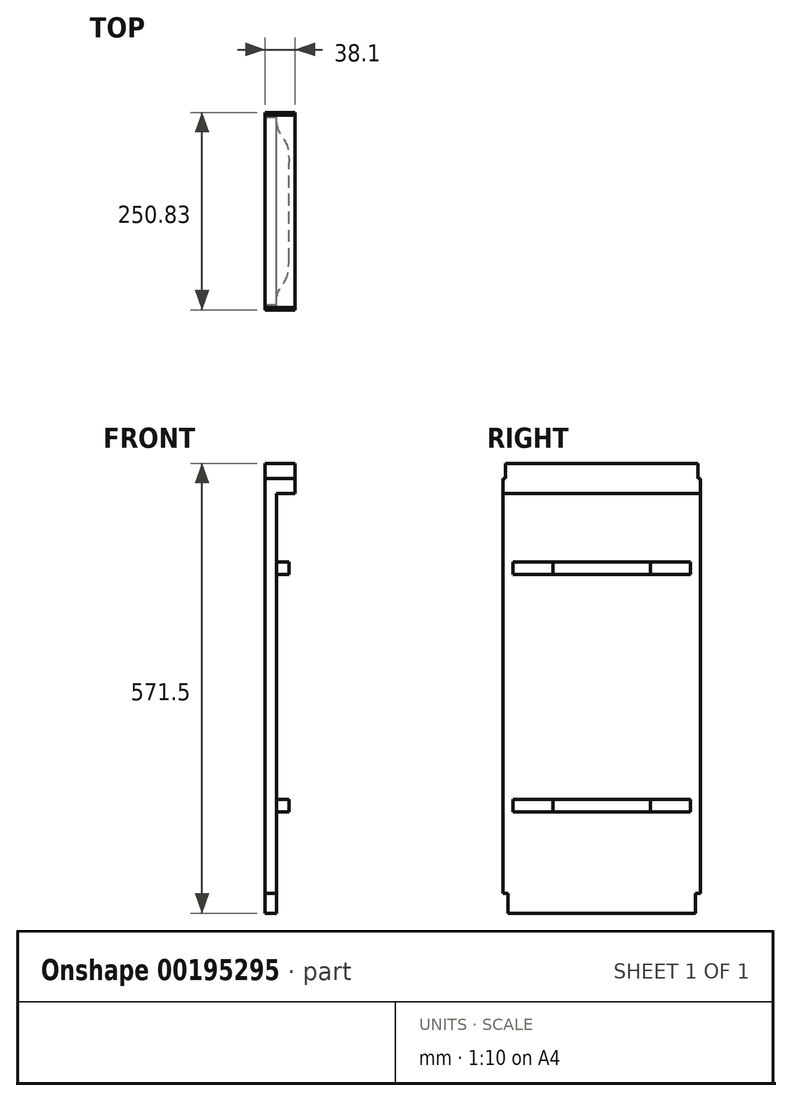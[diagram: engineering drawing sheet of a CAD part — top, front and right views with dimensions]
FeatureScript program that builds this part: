
annotation { "Feature Type Name" : "Feature", "Feature Type Description" : "" }
export const myFeature = defineFeature(function(context is Context, id is Id, definition is map)
    precondition{}
    {
        {
            var Q0;
            Q0=qCreatedBy(makeId("Front.planeOp"),FACE);
            var sketch = newSketch(context, id + "F0", { "sketchPlane" : qUnion([Q0])});
            skLineSegment(sketch, "E0.bottom", {"start": v(0, 0) * mm, "end": v(-14.29, 0) * mm});
            skLineSegment(sketch, "E0.top", {"start": v(0, 552.45) * mm, "end": v(-14.29, 552.45) * mm});
            skLineSegment(sketch, "E0.left", {"start": v(0, 0) * mm, "end": v(0, 552.45) * mm});
            skLineSegment(sketch, "E0.right", {"start": v(-14.29, 0) * mm, "end": v(-14.29, 552.45) * mm});
            skLineSegment(sketch, "E1.bottom", {"start": v(-14.29, 571.5) * mm, "end": v(23.81, 571.5) * mm});
            skLineSegment(sketch, "E1.top", {"start": v(0, 533.4) * mm, "end": v(23.81, 533.4) * mm});
            skLineSegment(sketch, "E1.left", {"start": v(-14.29, 571.5) * mm, "end": v(-14.29, 552.45) * mm});
            skLineSegment(sketch, "E1.right", {"start": v(23.81, 571.5) * mm, "end": v(23.81, 533.4) * mm});
            skLineSegment(sketch, "E2.bottom", {"start": v(0, 446.09) * mm, "end": v(15.87, 446.09) * mm});
            skLineSegment(sketch, "E2.top", {"start": v(0, 430.21) * mm, "end": v(15.87, 430.21) * mm});
            skLineSegment(sketch, "E2.left", {"start": v(0, 446.09) * mm, "end": v(0, 430.21) * mm});
            skLineSegment(sketch, "E2.right", {"start": v(15.87, 446.09) * mm, "end": v(15.87, 430.21) * mm});
            skLineSegment(sketch, "E3.bottom", {"start": v(0, 144.46) * mm, "end": v(15.88, 144.46) * mm});
            skLineSegment(sketch, "E3.top", {"start": v(0, 128.59) * mm, "end": v(15.88, 128.59) * mm});
            skLineSegment(sketch, "E3.left", {"start": v(0, 144.46) * mm, "end": v(0, 128.59) * mm});
            skLineSegment(sketch, "E3.right", {"start": v(15.88, 144.46) * mm, "end": v(15.88, 128.59) * mm});
            skPoint(sketch, "E4", {"position": v(0, 317.5) * mm});
            skLineSegment(sketch, "E5", {"start": v(0, 136.52) * mm, "end": v(15.88, 136.52) * mm, "construction": true});
            skLineSegment(sketch, "E6", {"start": v(0, 438.15) * mm, "end": v(15.87, 438.15) * mm, "construction": true});
            skSolve(sketch);
        }
        {
            var Q0;
            {var subQ1=sQuery(id+"F0.wireOp",EDGE,"E0.top");Q0=makeQuery(id+"F0.imprint","IMPRINT",FACE,{"disambiguationData":[TD([[makeQuery(id+"F0.imprint","IMPRINT",EDGE,{"derivedFrom":subQ1}),-1.0]])]});}
            var Q1;
            Q1=makeQuery(id+"F0.imprint","IMPRINT",FACE,{"disambiguationData":[TD([[makeQuery(id+"F0.imprint","IMPRINT",EDGE,{"derivedFrom":sQuery(id+"F0.wireOp",EDGE,"E2.bottom")}),-1.0]])]});
            var Q2;
            {var subQ3=sQuery(id+"F0.wireOp",EDGE,"E0.bottom");Q2=makeQuery(id+"F0.imprint","IMPRINT",FACE,{"disambiguationData":[TD([[makeQuery(id+"F0.imprint","IMPRINT",EDGE,{"derivedFrom":subQ3}),-1.0]])]});}
            var Q3;
            Q3=makeQuery(id+"F0.imprint","IMPRINT",FACE,{"disambiguationData":[TD([[makeQuery(id+"F0.imprint","IMPRINT",EDGE,{"derivedFrom":sQuery(id+"F0.wireOp",EDGE,"E3.bottom")}),-1.0]])]});
            extrude(context, id + "F1", {"entities" : qUnion([Q0, Q1, Q2, Q3]), "depth" : 250.82 * mm});
        }
        {
            var Q0;
            Q0=makeQuery(id+"F1.opExtrude","SWEPT_FACE",FACE,{"disambiguationData":[OSD([sQuery(id+"F0.wireOp",EDGE,"E0.right"),sQuery(id+"F0.wireOp",EDGE,"E1.left")])]});
            var sketch = newSketch(context, id + "F2", { "sketchPlane" : qUnion([Q0])});
            skLineSegment(sketch, "E7.bottom", {"start": v(0, 571.5) * mm, "end": v(3.18, 571.5) * mm});
            skLineSegment(sketch, "E7.top", {"start": v(0, 552.45) * mm, "end": v(3.18, 552.45) * mm});
            skLineSegment(sketch, "E7.left", {"start": v(0, 571.5) * mm, "end": v(0, 552.45) * mm});
            skLineSegment(sketch, "E7.right", {"start": v(3.18, 571.5) * mm, "end": v(3.18, 552.45) * mm});
            skLineSegment(sketch, "E8.bottom", {"start": v(250.83, 571.5) * mm, "end": v(247.65, 571.5) * mm});
            skLineSegment(sketch, "E8.top", {"start": v(250.83, 552.45) * mm, "end": v(247.65, 552.45) * mm});
            skLineSegment(sketch, "E8.left", {"start": v(250.83, 571.5) * mm, "end": v(250.83, 552.45) * mm});
            skLineSegment(sketch, "E8.right", {"start": v(247.65, 571.5) * mm, "end": v(247.65, 552.45) * mm});
            skLineSegment(sketch, "E9.bottom", {"start": v(6.35, 0) * mm, "end": v(0, 0) * mm});
            skLineSegment(sketch, "E9.top", {"start": v(6.35, 25.4) * mm, "end": v(0, 25.4) * mm});
            skLineSegment(sketch, "E9.left", {"start": v(6.35, 0) * mm, "end": v(6.35, 25.4) * mm});
            skLineSegment(sketch, "E9.right", {"start": v(0, 0) * mm, "end": v(0, 25.4) * mm});
            skLineSegment(sketch, "E10.bottom", {"start": v(250.83, 0) * mm, "end": v(244.48, 0) * mm});
            skLineSegment(sketch, "E10.top", {"start": v(250.83, 25.4) * mm, "end": v(244.48, 25.4) * mm});
            skLineSegment(sketch, "E10.left", {"start": v(250.83, 0) * mm, "end": v(250.83, 25.4) * mm});
            skLineSegment(sketch, "E10.right", {"start": v(244.48, 0) * mm, "end": v(244.48, 25.4) * mm});
            skSolve(sketch);
        }
        {
            var Q0;
            Q0=makeQuery(id+"F1.opExtrude","SWEPT_FACE",FACE,{"disambiguationData":[OSD([sQuery(id+"F0.wireOp",EDGE,"E3.top")])]});
            var sketch = newSketch(context, id + "F3", { "sketchPlane" : qUnion([Q0])});
            skPoint(sketch, "E11", {"position": v(15.88, 187.33) * mm});
            skPoint(sketch, "E12", {"position": v(15.88, 63.5) * mm});
            skPoint(sketch, "E13", {"position": v(15.88, 125.41) * mm});
            skLineSegment(sketch, "E14", {"start": v(15.88, 125.41) * mm, "end": v(0, 125.41) * mm, "construction": true});
            skPoint(sketch, "E15", {"position": v(0, 238.13) * mm});
            skPoint(sketch, "E16", {"position": v(0, 6.35) * mm});
            skFitSpline(sketch, "E17", {"points": [v(0, 238.13) * mm, v(2.75, 227.35) * mm, v(7.17, 219.85) * mm, v(9.83, 216.04) * mm, v(13.62, 208.32) * mm, v(15.88, 187.33) * mm], "startDerivative": vector(9.95, -52.63) * mm, "endDerivative": vector(3.27, -99.16) * mm});
            skFitSpline(sketch, "E18.MirrorCS", {"points": [v(0, 12.7) * mm, v(2.75, 23.48) * mm, v(7.17, 30.98) * mm, v(9.83, 34.79) * mm, v(13.62, 42.5) * mm, v(15.88, 63.5) * mm], "startDerivative": vector(9.95, 52.63) * mm, "endDerivative": vector(3.27, 99.16) * mm});
            skSolve(sketch);
        }
        {
            var Q0;
            {var subQ0=sQuery(id+"F3.wireOp",EDGE,"E17");Q0=makeQuery(id+"F3.imprint","IMPRINT",FACE,{"disambiguationData":[TD([[makeQuery(id+"F3.imprint","IMPRINT",EDGE,{"derivedFrom":subQ0}),1.0]])]});}
            var Q1;
            {var subQ0=sQuery(id+"F3.wireOp",EDGE,"E18.MirrorCS");Q1=makeQuery(id+"F3.imprint","IMPRINT",FACE,{"disambiguationData":[TD([[makeQuery(id+"F3.imprint","IMPRINT",EDGE,{"derivedFrom":subQ0}),-1.0]])]});}
            var Q2;
            Q2=makeQuery(id+"F1.opExtrude","SWEPT_FACE",FACE,{"disambiguationData":[OSD([sQuery(id+"F0.wireOp",EDGE,"E2.bottom")])]});
            extrude(context, id + "F4", {"entities" : qUnion([Q0, Q1]), "operationType" : NewBodyOperationType.REMOVE, "endBound" : BoundingType.UP_TO_SURFACE, "oppositeDirection" : true, "endBoundEntityFace" : qUnion([Q2]), "depth" : 330.2 * mm});
        }
        {
            var Q0;
            Q0=makeQuery(id+"F2.imprint","IMPRINT",FACE,{"disambiguationData":[TD([[makeQuery(id+"F2.imprint","IMPRINT",EDGE,{"derivedFrom":sQuery(id+"F2.wireOp",EDGE,"E9.bottom")}),-1.0]])]});
            var Q1;
            Q1=makeQuery(id+"F2.imprint","IMPRINT",FACE,{"disambiguationData":[TD([[makeQuery(id+"F2.imprint","IMPRINT",EDGE,{"derivedFrom":sQuery(id+"F2.wireOp",EDGE,"E10.bottom")}),-1.0]])]});
            var Q2;
            Q2=makeQuery(id+"F2.imprint","IMPRINT",FACE,{"disambiguationData":[TD([[makeQuery(id+"F2.imprint","IMPRINT",EDGE,{"derivedFrom":sQuery(id+"F2.wireOp",EDGE,"E8.bottom")}),1.0]])]});
            var Q3;
            Q3=makeQuery(id+"F2.imprint","IMPRINT",FACE,{"disambiguationData":[TD([[makeQuery(id+"F2.imprint","IMPRINT",EDGE,{"derivedFrom":sQuery(id+"F2.wireOp",EDGE,"E7.bottom")}),1.0]])]});
            extrude(context, id + "F5", {"entities" : qUnion([Q0, Q1, Q2, Q3]), "operationType" : NewBodyOperationType.REMOVE, "endBound" : BoundingType.THROUGH_ALL, "oppositeDirection" : true, "depth" : 25.4 * mm});
        }
    });
